# Revit family: Mini HYde_LBA_SbD
name_source: partatom
category: Equipement spécialisé
revit_build: Autodesk Revit 2017 (Build: 20190508_0315(x64)
units: mm (PartAtom-declared; Revit-internal decimal feet)

## family parameters
Basée sur le plan de construction = Non
Cote de connecteur circulaire = Utiliser le diamètre
Couper avec des vides une fois chargée = Non
Partagée = Non
Point de calcul de pièce = Non
Toujours verticalement = Oui
Type d'élément = Normal

## types (1)
- Mini HYde
    Fabricant = La Barrière Automatique – Security by Design
    H2 = 612 mm  [stored 2.00787 ft]
    Matériau_Haut = MATERIAU BLANC
    Matériau_corps = PIERRE GRISE
    Modèle = Mini HYde
    URL = https://barriere-automatique.com
    hauteur = 270 mm  [stored 0.885827 ft]
    hauteur_base = 270 mm  [stored 0.885827 ft]
    hauteur_corps = 342 mm  [stored 1.12205 ft]
    largeur = 200 mm  [stored 0.656168 ft]
    longueur = 330 mm  [stored 1.08268 ft]

note: [stored X ft] marks values corroborated as IEEE doubles in the binary element streams (Revit-internal decimal feet)
